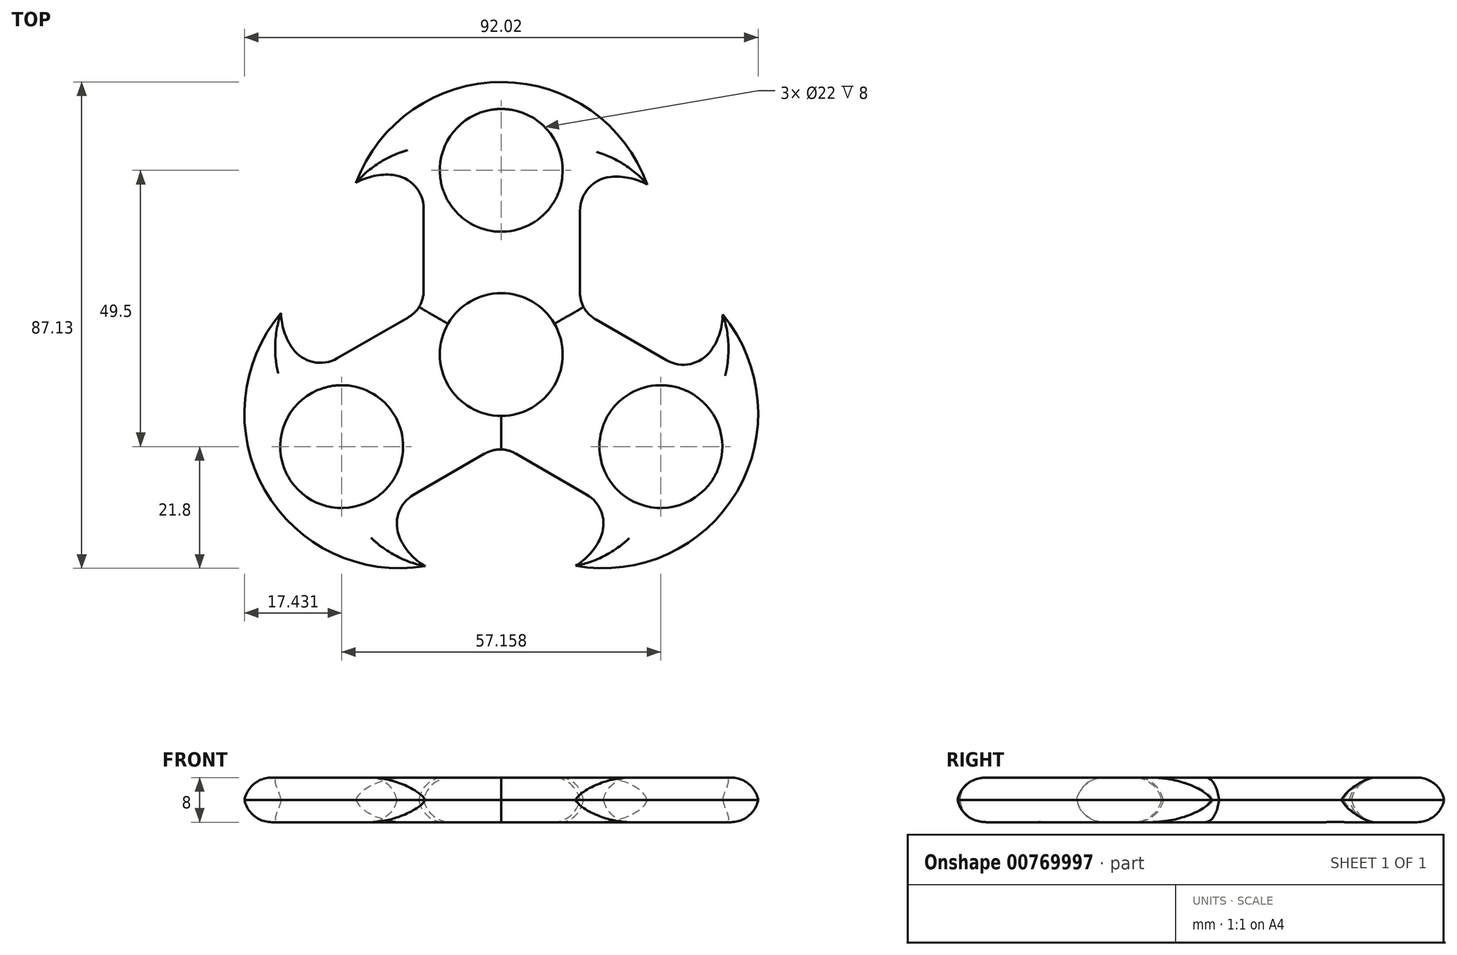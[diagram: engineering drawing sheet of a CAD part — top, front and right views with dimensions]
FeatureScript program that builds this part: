
annotation { "Feature Type Name" : "Feature", "Feature Type Description" : "" }
export const myFeature = defineFeature(function(context is Context, id is Id, definition is map)
    precondition{}
    {
        {
            var Q0;
            Q0=qCreatedBy(makeId("Top.planeOp"),FACE);
            var sketch = newSketch(context, id + "F0", { "sketchPlane" : qUnion([Q0])});
            skCircle(sketch, "E0", {"center": v(0, 33) * mm, "radius": 11 * mm});
            skLineSegment(sketch, "E1", {"start": v(0, 33) * mm, "end": v(0, 0) * mm, "construction": true});
            skLineSegment(sketch, "E2", {"start": v(-14, 26.1) * mm, "end": v(-14, 11.55) * mm});
            skLineSegment(sketch, "E3", {"start": v(14.2, 25.74) * mm, "end": v(14.2, 11.19) * mm});
            skPoint(sketch, "E4.visualSharp", {"position": v(-14, 8.08) * mm});
            skArc(sketch, "E4.filletArc", {"start": v(-14.8, 8.55) * mm, "mid": v(-14.2, 10) * mm, "end": v(-14, 11.55) * mm});
            skPoint(sketch, "E5.visualSharp", {"position": v(14.2, 7.72) * mm});
            skArc(sketch, "E5.filletArc", {"start": v(14.2, 11.19) * mm, "mid": v(14.35, 9.83) * mm, "end": v(14.8, 8.55) * mm});
            skArc(sketch, "E6", {"start": v(26.33, 30.21) * mm, "mid": v(0.16, 48.93) * mm, "end": v(-26.22, 30.52) * mm});
            skArc(sketch, "E7", {"start": v(26.33, 30.21) * mm, "mid": v(23.08, 31.5) * mm, "end": v(19.6, 31.71) * mm});
            skArc(sketch, "E8", {"start": v(-19.4, 32.07) * mm, "mid": v(-22.93, 31.85) * mm, "end": v(-26.22, 30.52) * mm});
            skPoint(sketch, "E9.visualSharp", {"position": v(-14, 30) * mm});
            skArc(sketch, "E9.filletArc", {"start": v(-14, 26.1) * mm, "mid": v(-15.55, 30.13) * mm, "end": v(-19.4, 32.07) * mm});
            skPoint(sketch, "E10.visualSharp", {"position": v(14.2, 29.64) * mm});
            skArc(sketch, "E10.filletArc", {"start": v(19.6, 31.71) * mm, "mid": v(15.74, 29.77) * mm, "end": v(14.2, 25.74) * mm});
            skLineSegment(sketch, "E11", {"start": v(-14.8, 8.55) * mm, "end": v(-9.53, 5.5) * mm});
            skLineSegment(sketch, "E12", {"start": v(9.53, 5.5) * mm, "end": v(14.8, 8.55) * mm});
            skLineSegment(sketch, "E13", {"start": v(0, 0) * mm, "end": v(9.53, 5.5) * mm, "construction": true});
            skLineSegment(sketch, "E14", {"start": v(0, 0) * mm, "end": v(-9.53, 5.5) * mm, "construction": true});
            skArc(sketch, "E15", {"start": v(9.53, 5.5) * mm, "mid": v(0, 11) * mm, "end": v(-9.53, 5.5) * mm});
            skSolve(sketch);
        }
        {
            var Q0;
            Q0=qSketchRegion(id+"F0",true);
            extrude(context, id + "F1", {"entities" : qUnion([Q0]), "depth" : 7 * mm, "offsetDistance" : 25 * mm});
        }
        {
            var Q0;
            Q0 = qSketchRegion(id + "F0", true);
            extrude(context, id + "F2", {"entities" : qUnion([Q0]), "operationType" : NewBodyOperationType.ADD, "depth" : 8 * mm, "offsetDistance" : 25 * mm});
        }
        {
            var Q0;
            Q0=qCreatedBy(makeId("Front.planeOp"),FACE);
            var sketch = newSketch(context, id + "F3", { "sketchPlane" : qUnion([Q0])});
            skLineSegment(sketch, "E16", {"start": v(0, 0) * mm, "end": v(0, 19.1) * mm, "construction": true});
            skSolve(sketch);
        }
        {
            var Q0;
            Q0=makeQuery(id+"F1.opExtrude","SWEPT_BODY",BODY,{"disambiguationData":[OSD([sQuery(id+"F0.wireOp",EDGE,"E0"),sQuery(id+"F0.wireOp",EDGE,"E2"),sQuery(id+"F0.wireOp",EDGE,"E3"),sQuery(id+"F0.wireOp",EDGE,"E4.filletArc"),sQuery(id+"F0.wireOp",EDGE,"E5.filletArc"),sQuery(id+"F0.wireOp",EDGE,"E6"),sQuery(id+"F0.wireOp",EDGE,"E7"),sQuery(id+"F0.wireOp",EDGE,"E8"),sQuery(id+"F0.wireOp",EDGE,"E9.filletArc"),sQuery(id+"F0.wireOp",EDGE,"E10.filletArc"),sQuery(id+"F0.wireOp",EDGE,"E11"),sQuery(id+"F0.wireOp",EDGE,"E12"),sQuery(id+"F0.wireOp",EDGE,"itBTHJhJ-ycFz-TtXb-8W93-660oLclAuwB6")])]});
            var Q1;
            Q1=sQuery(id+"F3.wireOp",EDGE,"E16");
            circularPattern(context, id + "F4", {"entities" : qUnion([Q0]), "axis" : qUnion([Q1]), "angle" : 360 * degree, "instanceCount" : 3, "equalSpace" : true});
        }
        {
            var Q0;
            Q0=makeQuery(id+"F2.opExtrude","CAP_EDGE",EDGE,{"disambiguationData":[OSD([sQuery(id+"F0.wireOp",EDGE,"E2")])],"isStart":false});
            var Q1;
            Q1=makeQuery(id+"F1.opExtrude","CAP_EDGE",EDGE,{"disambiguationData":[OSD([sQuery(id+"F0.wireOp",EDGE,"E2")])],"isStart":true});
            var Q2;
            Q2=makeQuery(id+"F1.opExtrude","CAP_EDGE",EDGE,{"disambiguationData":[OSD([sQuery(id+"F0.wireOp",EDGE,"E3")])],"isStart":true});
            var Q3;
            Q3=makeQuery(id+"F4.opPattern","COPY",EDGE,{"derivedFrom":makeQuery(id+"F2.opExtrude","CAP_EDGE",EDGE,{"disambiguationData":[OSD([sQuery(id+"F0.wireOp",EDGE,"E4.filletArc")])],"isStart":false}),"instanceName":"2"});
            var Q4;
            Q4=makeQuery(id+"F1.opExtrude","CAP_EDGE",EDGE,{"disambiguationData":[OSD([sQuery(id+"F0.wireOp",EDGE,"E5.filletArc")])],"isStart":true});
            var Q5;
            Q5=makeQuery(id+"F4.opPattern","COPY",EDGE,{"derivedFrom":makeQuery(id+"F1.opExtrude","CAP_EDGE",EDGE,{"disambiguationData":[OSD([sQuery(id+"F0.wireOp",EDGE,"E4.filletArc")])],"isStart":true}),"instanceName":"2"});
            var Q6;
            Q6=makeQuery(id+"F4.opPattern","COPY",EDGE,{"derivedFrom":makeQuery(id+"F2.opExtrude","CAP_EDGE",EDGE,{"disambiguationData":[OSD([sQuery(id+"F0.wireOp",EDGE,"E3")])],"isStart":false}),"instanceName":"2"});
            var Q7;
            Q7=makeQuery(id+"F4.opPattern","COPY",EDGE,{"derivedFrom":makeQuery(id+"F1.opExtrude","CAP_EDGE",EDGE,{"disambiguationData":[OSD([sQuery(id+"F0.wireOp",EDGE,"E3")])],"isStart":true}),"instanceName":"2"});
            var Q8;
            Q8=makeQuery(id+"F4.opPattern","COPY",EDGE,{"derivedFrom":makeQuery(id+"F2.opExtrude","CAP_EDGE",EDGE,{"disambiguationData":[OSD([sQuery(id+"F0.wireOp",EDGE,"E2")])],"isStart":false}),"instanceName":"1"});
            var Q9;
            Q9=makeQuery(id+"F4.opPattern","COPY",EDGE,{"derivedFrom":makeQuery(id+"F1.opExtrude","CAP_EDGE",EDGE,{"disambiguationData":[OSD([sQuery(id+"F0.wireOp",EDGE,"E2")])],"isStart":true}),"instanceName":"1"});
            var Q10;
            Q10=makeQuery(id+"F4.opPattern","COPY",EDGE,{"derivedFrom":makeQuery(id+"F2.opExtrude","CAP_EDGE",EDGE,{"disambiguationData":[OSD([sQuery(id+"F0.wireOp",EDGE,"E3")])],"isStart":false}),"instanceName":"1"});
            var Q11;
            Q11=makeQuery(id+"F4.opPattern","COPY",EDGE,{"derivedFrom":makeQuery(id+"F1.opExtrude","CAP_EDGE",EDGE,{"disambiguationData":[OSD([sQuery(id+"F0.wireOp",EDGE,"E3")])],"isStart":true}),"instanceName":"1"});
            var Q12;
            Q12=makeQuery(id+"F4.opPattern","COPY",EDGE,{"derivedFrom":makeQuery(id+"F2.opExtrude","CAP_EDGE",EDGE,{"disambiguationData":[OSD([sQuery(id+"F0.wireOp",EDGE,"E6")])],"isStart":false}),"instanceName":"1"});
            var Q13;
            Q13=makeQuery(id+"F4.opPattern","COPY",EDGE,{"derivedFrom":makeQuery(id+"F1.opExtrude","CAP_EDGE",EDGE,{"disambiguationData":[OSD([sQuery(id+"F0.wireOp",EDGE,"E6")])],"isStart":true}),"instanceName":"1"});
            var Q14;
            Q14=makeQuery(id+"F4.opPattern","COPY",EDGE,{"derivedFrom":makeQuery(id+"F2.opExtrude","CAP_EDGE",EDGE,{"disambiguationData":[OSD([sQuery(id+"F0.wireOp",EDGE,"E6")])],"isStart":false}),"instanceName":"2"});
            var Q15;
            Q15=makeQuery(id+"F4.opPattern","COPY",EDGE,{"derivedFrom":makeQuery(id+"F1.opExtrude","CAP_EDGE",EDGE,{"disambiguationData":[OSD([sQuery(id+"F0.wireOp",EDGE,"E6")])],"isStart":true}),"instanceName":"2"});
            var Q16;
            Q16=makeQuery(id+"F2.opExtrude","CAP_EDGE",EDGE,{"disambiguationData":[OSD([sQuery(id+"F0.wireOp",EDGE,"E6")])],"isStart":false});
            var Q17;
            Q17=makeQuery(id+"F1.opExtrude","CAP_EDGE",EDGE,{"disambiguationData":[OSD([sQuery(id+"F0.wireOp",EDGE,"E6")])],"isStart":true});
            var Q18;
            Q18=makeQuery(id+"F2.opExtrude","CAP_EDGE",EDGE,{"disambiguationData":[OSD([sQuery(id+"F0.wireOp",EDGE,"E3")])],"isStart":false});
            fillet(context, id + "F5", {"entities" : qUnion([Q0, Q1, Q2, Q3, Q4, Q5, Q6, Q7, Q8, Q9, Q10, Q11, Q12, Q13, Q14, Q15, Q16, Q17, Q18]), "radius" : 5 * mm, "tangentPropagation" : true, "allowEdgeOverflow" : false});
        }
    });
